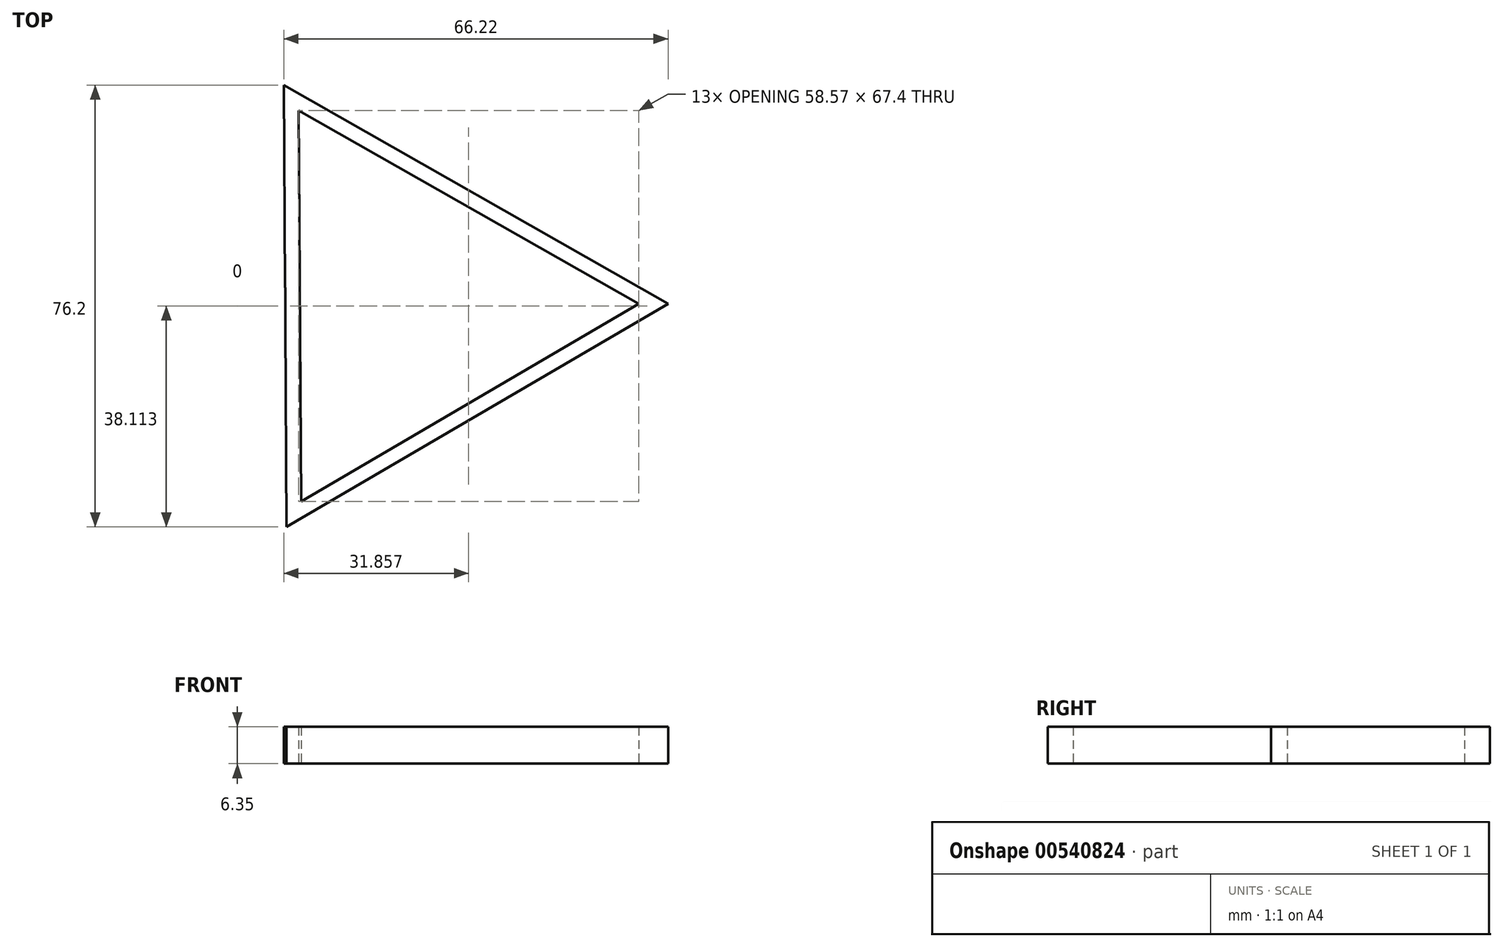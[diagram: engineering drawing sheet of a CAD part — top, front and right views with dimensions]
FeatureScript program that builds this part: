
annotation { "Feature Type Name" : "Feature", "Feature Type Description" : "" }
export const myFeature = defineFeature(function(context is Context, id is Id, definition is map)
    precondition{}
    {
        {
            var Q0;
            Q0=qCreatedBy(makeId("Top.planeOp"),FACE);
            var sketch = newSketch(context, id + "F0", { "sketchPlane" : qUnion([Q0])});
            skCircle(sketch, "E0.cCircle", {"center": v(0, 0) * mm, "radius": 22 * mm, "construction": true});
            skLineSegment(sketch, "E0.0", {"start": v(-22.23, 37.97) * mm, "end": v(44, 0.26) * mm});
            skLineSegment(sketch, "E0.1", {"start": v(44, 0.26) * mm, "end": v(-21.77, -38.23) * mm});
            skLineSegment(sketch, "E0.2", {"start": v(-21.77, -38.23) * mm, "end": v(-22.23, 37.97) * mm});
            skPoint(sketch, "E0.0.midPoint", {"position": v(10.88, 19.12) * mm});
            skLineSegment(sketch, "E1.0", {"start": v(-19.25, -33.82) * mm, "end": v(-19.66, 33.58) * mm});
            skLineSegment(sketch, "E1.1", {"start": v(38.91, 0.23) * mm, "end": v(-19.25, -33.82) * mm});
            skLineSegment(sketch, "E1.2", {"start": v(-19.66, 33.58) * mm, "end": v(38.91, 0.23) * mm});
            skLineSegment(sketch, "E2.bottom", {"start": v(-21.98, -3.3) * mm, "end": v(-28.33, -3.3) * mm});
            skLineSegment(sketch, "E2.top", {"start": v(-21.98, 3.04) * mm, "end": v(-28.33, 3.04) * mm});
            skLineSegment(sketch, "E2.left", {"start": v(-21.98, -3.3) * mm, "end": v(-21.98, 3.04) * mm});
            skLineSegment(sketch, "E2.right", {"start": v(-28.33, -3.3) * mm, "end": v(-28.33, 3.04) * mm});
            skSolve(sketch);
        }
        {
            var Q0;
            Q0=makeQuery(id+"F0.imprint","IMPRINT",FACE,{"disambiguationData":[TD([[makeQuery(id+"F0.imprint","IMPRINT",EDGE,{"derivedFrom":sQuery(id+"F0.wireOp",EDGE,"E0.0")}),-1.0]])]});
            extrude(context, id + "F1", {"entities" : qUnion([Q0]), "depth" : 6.35 * mm, "offsetDistance" : 25.4 * mm});
        }
    });
